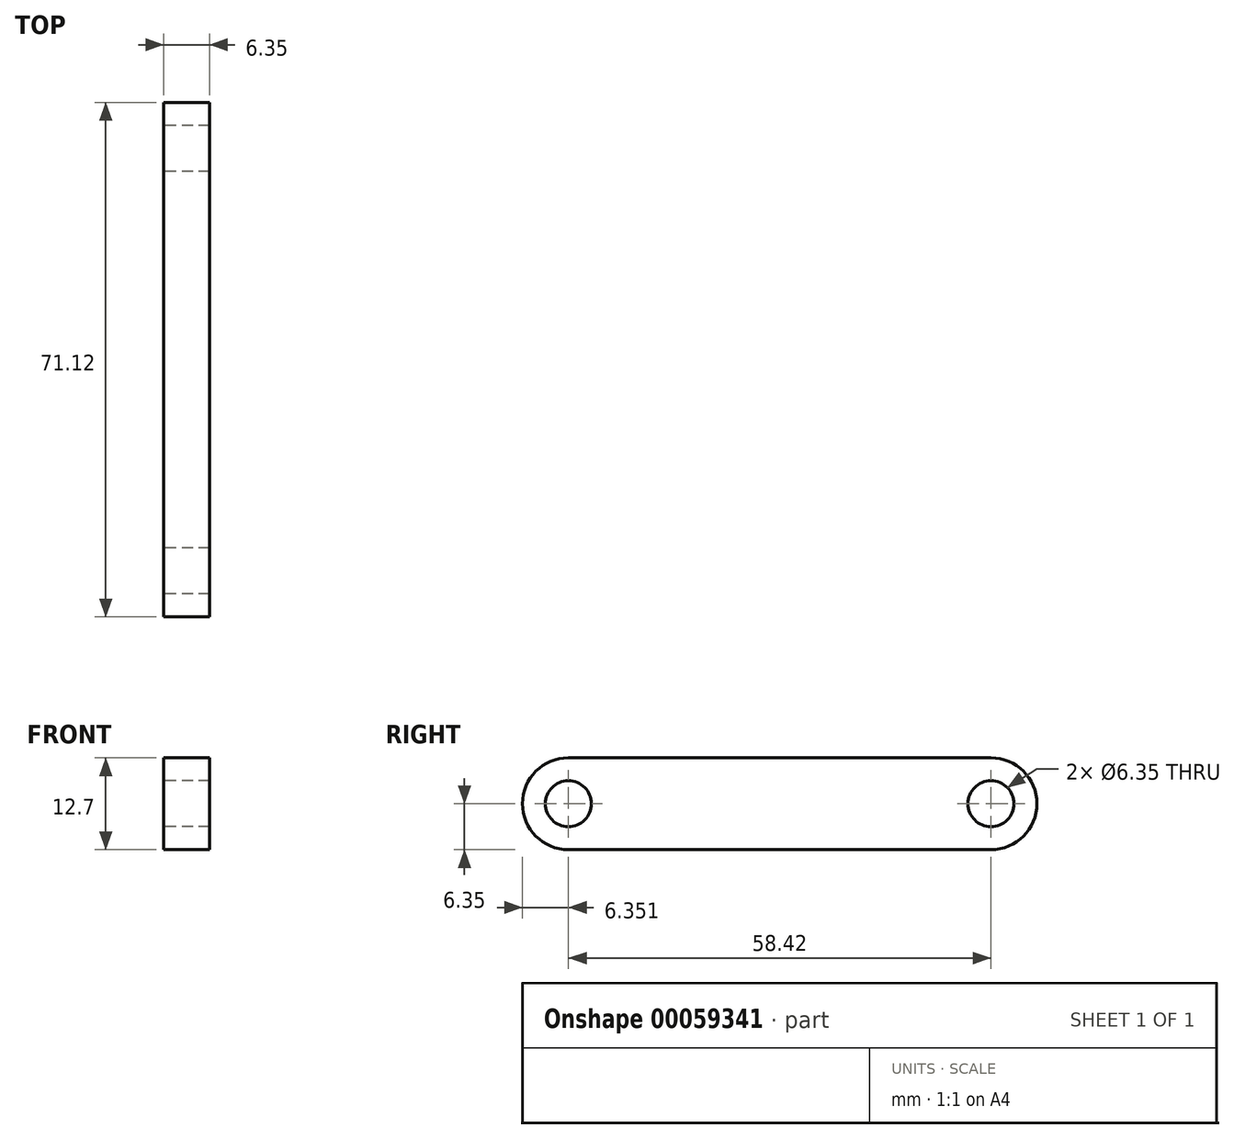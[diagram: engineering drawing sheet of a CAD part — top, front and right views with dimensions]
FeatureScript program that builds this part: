
annotation { "Feature Type Name" : "Feature", "Feature Type Description" : "" }
export const myFeature = defineFeature(function(context is Context, id is Id, definition is map)
    precondition{}
    {
        {
            var Q0;
            Q0=qCreatedBy(makeId("Right.planeOp"),FACE);
            var sketch = newSketch(context, id + "F0", { "sketchPlane" : qUnion([Q0])});
            skLineSegment(sketch, "E0.bottom", {"start": v(-28.35, 5.43) * mm, "end": v(30.07, 5.43) * mm});
            skLineSegment(sketch, "E0.top", {"start": v(-28.35, -7.27) * mm, "end": v(30.07, -7.27) * mm});
            skArc(sketch, "E1", {"start": v(-28.35, 5.43) * mm, "mid": v(-34.7, -0.92) * mm, "end": v(-28.35, -7.27) * mm});
            skArc(sketch, "E2", {"start": v(30.07, -7.27) * mm, "mid": v(36.42, -0.92) * mm, "end": v(30.07, 5.43) * mm});
            skCircle(sketch, "E3", {"center": v(-28.35, -0.92) * mm, "radius": 3.18 * mm});
            skCircle(sketch, "E4", {"center": v(30.07, -0.92) * mm, "radius": 3.18 * mm});
            skSolve(sketch);
        }
        {
            var Q0;
            Q0=makeQuery(id+"F0.imprint","IMPRINT",FACE,{"disambiguationData":[TD([[makeQuery(id+"F0.imprint","IMPRINT",EDGE,{"derivedFrom":sQuery(id+"F0.wireOp",EDGE,"E0.bottom")}),-1.0]])]});
            extrude(context, id + "F1", {"entities" : qUnion([Q0]), "depth" : 6.35 * mm});
        }
    });
